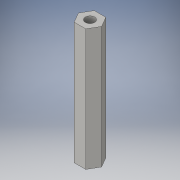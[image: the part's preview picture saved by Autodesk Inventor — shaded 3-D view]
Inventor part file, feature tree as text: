
AUTODESK INVENTOR PART (.ipt)
format: ipt  version: 2016 (Build 200138000, 138)  size: 93,184 bytes
history: native  units: in
note: dims shown in document units (in); Inventor stores cm internally (conversion verified against a paired STEP export)
features: extrude x1, sketch x1
ambient origin geometry x8: Origin, YZ Plane, XZ Plane, XY Plane, X Axis, Y Axis, Z Axis, Center Point
bodies: Solid1 (feature_tree)
feature tree (2):
  extrude  "Extrusion1"  Depth=3.0in
  sketch  "Sketch1"  dims[d0=0.231in d1=0.2475in d2=3.0in d3=0.0in]
